# Revit family: Legrand_Lighting_Management_Standalone_Presence_Sensor_Wall
name_source: partatom
category: Dispositifs d'éclairage
units: mm (PartAtom-declared; Revit-internal decimal feet)

## family parameters
Conserver l'orientation des annotations = Oui
Cote de connecteur circulaire = Utiliser le diamètre
Couper avec des vides une fois chargée = Non
Hôte = Face
Partagée = Non
Point de calcul de pièce = Non
Type d'élément = Normal

## types (4) — shared parameters
Collecteur de terre = Non
Colour = White
Constant light control = Oui
Cosses d'artère secondaire = Non
Elévation par défaut = 2500 mm  [stored 8.2021 ft]
Fabricant = Legrand
Frequency (MAX) (Hz) = 60
Frequency (MIN) (Hz) = 50
General Conditions of Use = https://export.legrand.com
HVAC-control = Non
Liaison neutre = Non
Maximum mounting height (m) = 2.5
Min. switch-on time (s) = 5
Nominal voltage (V) = 230
Remote operation = Oui
Response value luminosity adjustable = Oui
Response value sensitivity adjustable = Oui
Temperature (MAX) (°C) = 45
Temperature (MIN) (°C) = -5
URL = http://www.legrandoc.com

## per-type parameters (varying)
- IP42 ECO 2 PIR/US: Alarm function=Non; Couloir=Non; Degree of protection (IP)=IP42; Description=180° surface sensor - Dual technology - range 8 m - with presence output - white; Detection angle horizontal (MAX) (°)=180; Detection angle horizontal (MIN) (°)=180; Diameter detection range on floor (m)=12; Dim function with dimmer basic element=Oui; Forced switch off=Oui; IP 42 - Modelisation 9=Non; IP42 ECO 2 PIR/US=Oui; IP55 ECO 2=Non; Max. duty cycle (mn)=60; Max. starting current (A)=0; Max. switching power (W)=0; Max. transmission range frontally (m)=8; Max. transmission range sideways (m)=8; Model=Presence detector; Modèle=048916; Mounting method=Flush mounted (plaster); RAL-number (akin)=9006; Response value luminosity (MAX) (lx)=1275; Response value luminosity (MIN) (lx)=5; Substation input=Non; Suitable for wireless transmission=Oui
- IP55 ECO 2: Alarm function=Oui; Couloir=Non; Degree of protection (IP)=IP55; Description=Lighting management-traffic detection-ceiling mounting- IR - 270°- range 18 m; Detection angle horizontal (MAX) (°)=360; Detection angle horizontal (MIN) (°)=0; Diameter detection range on floor (m)=8; Dim function with dimmer basic element=Non; Forced switch off=Non; IP 42 - Modelisation 9=Non; IP42 ECO 2 PIR/US=Non; IP55 ECO 2=Oui; Max. duty cycle (mn)=59; Max. starting current (A)=8.5; Max. switching power (W)=2000; Max. transmission range frontally (m)=15; Max. transmission range sideways (m)=5; Model=Movement sensor; Modèle=048933; Mounting method=Surface mounted (plaster); RAL-number (akin)=9003; Response value luminosity (MAX) (lx)=1275; Response value luminosity (MIN) (lx)=5; Substation input=Oui; Suitable for wireless transmission=Non; Voltage type=AC
- IP42: Alarm function=Non; Couloir=Non; Degree of protection (IP)=IP42; Description=180° surface sensor - PIR technology - range 8 m - with presence output - white; Detection angle horizontal (MAX) (°)=180; Detection angle horizontal (MIN) (°)=180; Diameter detection range on floor (m)=12; Dim function with dimmer basic element=Oui; Forced switch off=Oui; IP 42 - Modelisation 9=Oui; IP42 ECO 2 PIR/US=Non; IP55 ECO 2=Non; Max. duty cycle (mn)=60; Max. starting current (A)=0; Max. switching power (W)=0; Max. transmission range frontally (m)=20; Max. transmission range sideways (m)=12; Model=Presence detector; Modèle=048914; Mounting method=Flush mounted (plaster); RAL-number (akin)=9006; Response value luminosity (MAX) (lx)=1000; Response value luminosity (MIN) (lx)=1; Substation input=Non; Suitable for wireless transmission=Oui
- IP42 ECO corridor: Alarm function=Non; Couloir=Oui; Degree of protection (IP)=IP42; Description=Lighting management-traffic detection-surface mounting- IR - 180°- range 15 m; Detection angle horizontal (MAX) (°)=180; Detection angle horizontal (MIN) (°)=180; Diameter detection range on floor (m)=12; Dim function with dimmer basic element=Oui; Forced switch off=Oui; IP 42 - Modelisation 9=Oui; IP42 ECO 2 PIR/US=Non; IP55 ECO 2=Non; Max. duty cycle (mn)=60; Max. starting current (A)=0; Max. switching power (W)=0; Max. transmission range frontally (m)=20; Max. transmission range sideways (m)=12; Model=Presence detector; Modèle=048917; Mounting method=Flush mounted (plaster); RAL-number (akin)=9006; Response value luminosity (MAX) (lx)=1275; Response value luminosity (MIN) (lx)=5; Substation input=Non; Suitable for wireless transmission=Oui

note: [stored X ft] marks values corroborated as IEEE doubles in the binary element streams (Revit-internal decimal feet)
